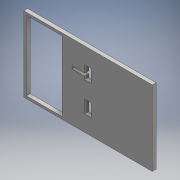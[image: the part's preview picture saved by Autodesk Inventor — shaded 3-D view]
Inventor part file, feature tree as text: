
AUTODESK INVENTOR PART (.ipt)
format: ipt  version: 2016 (Build 200138000, 138)  size: 121,856 bytes
history: native  units: mm
features: extrude x1, sketch x1
ambient origin geometry x8: Origin, YZ Plane, XZ Plane, XY Plane, X Axis, Y Axis, Z Axis, Center Point
bodies: Body1 (feature_tree)
feature tree (2):
  extrude  "Extrusion2"  Depth=59.0mm
  sketch  "Sketch1"  dims[d0=101.0mm d1=59.0mm d7=5.0mm d8=10.0mm d9=5.0mm d10=10.0mm d11=10.0mm d12=2.0mm d13=3.0mm d14=0.0mm d16=2.0mm d17=2.0mm d18=2.0mm d19=28.0mm d20=20.0mm]
